# Revit family: LE-138-15
name_source: partatom
category: Plumbing Fixtures
revit_build: Autodesk Revit Architecture 2012 (Build: 20110309_2315(x64)
units: mm (PartAtom-declared; Revit-internal decimal feet)

## types (1)
- LE-138-15
    Assembly Code = D2010
    Brass compression ring = D-65XS-15
    CW Connection = No
    CWFU = 0
    Compression capnut = 64XS-15
    Cost = 0 $
    Default Elevation = 0' - 0"
    Description = 1 pair undertile with 15mm copper inlets
    HW Connection = No
    HWFU = 0
    Headpart anti-clockwise closing = S-21-2ANTI
    Headpart clockwise closing = S-21-1CLOCK
    Keynote = 1/4 turn ceramic disk headparts (1 x Anti clockwise closing, 1 x Clockwise closing)
    Manufacturer = COBRA
    Material = Chrome - Polished
    Model = LE-138-15
    Range = Leading Edge
    Type Comments = SANS 226 type 2
    URL = http://www.cobra.co.za Edge&Section=Bathroom
    Vent Connection = No
    WFU = 0
    Waste Connection = No

## geometry (parser evidence)
native form markers: Blend x2
no freeform markers — native parametric forms only
